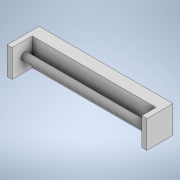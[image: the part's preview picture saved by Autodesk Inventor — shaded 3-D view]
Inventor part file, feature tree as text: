
AUTODESK INVENTOR PART (.ipt)
format: ipt  version: 2022 (Build 260153000, 153)  size: 135,680 bytes
history: native  units: in
note: dims shown in document units (in); Inventor stores cm internally (conversion verified against a paired STEP export)
features: extrude x5, sketch x2, thread x2
ambient origin geometry x8: Origin, YZ Plane, XZ Plane, XY Plane, X Axis, Y Axis, Z Axis, Center Point
bodies: Solid1 (feature_tree)
feature tree (9):
  extrude  "Extrusion1"  Depth=1.1811in
  sketch  "Sketch2"  dims[d2=0.5118in d3=0.0in d4=0.2165in d5=0.2165in d6=0.8661in d7=0.0in d8=0.6102in d9=0.0in d10=0.3543in d11=2.0079in d12=0.0in d13=4.8819in d14=0.0in d21=0.374in d22=0.1575in d23=0.6102in d24=0.0in d25=5.315in d26=0.0in]
  extrude  "Extrusion2"  Depth=0.2165in
  extrude  "Extrusion3"  Depth=0.2165in
  extrude  "Extrusion7"  Depth=0.8661in TaperAngle=0.0deg
  thread  "Thread2"  [1 undecoded]
  extrude  "Extrusion4"  Depth=5.315in
  thread  "Thread1"  [1 undecoded]
  sketch  "Sketch1"  dims[d0=5.748in d1=1.1811in]
note: 2 required parameter values undecoded (feature->parameter linkage not recoverable at this tier; creation-order binding heuristic only, values carry confidence <= 0.55)
